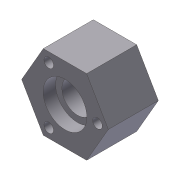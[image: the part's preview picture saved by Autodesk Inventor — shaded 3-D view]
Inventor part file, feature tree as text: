
AUTODESK INVENTOR PART (.ipt)
format: ipt  version: 2012 (Build 160160000, 160)  size: 110,080 bytes
history: native  units: in
note: dims shown in document units (in); Inventor stores cm internally (conversion verified against a paired STEP export)
features: extrude x3, sketch x3
ambient origin geometry x8: Origin, YZ Plane, XZ Plane, XY Plane, X Axis, Y Axis, Z Axis, Center Point
bodies: Solid1 (feature_tree)
feature tree (6):
  extrude  "Extrusion1"  Depth=1.5in
  extrude  "Extrusion2"  Depth=0.192in
  extrude  "Extrusion3"  Depth=0.875in
  sketch  "Sketch1"  dims[d0=0.625in d1=1.5in]
  sketch  "Sketch2"  dims[d2=1.125in d3=0.192in]
  sketch  "Sketch3"  dims[d4=1.0in d5=0.0in d6=0.875in d7=0.25in d8=0.0in d9=0.875in d10=0.25in d11=0.0in]
